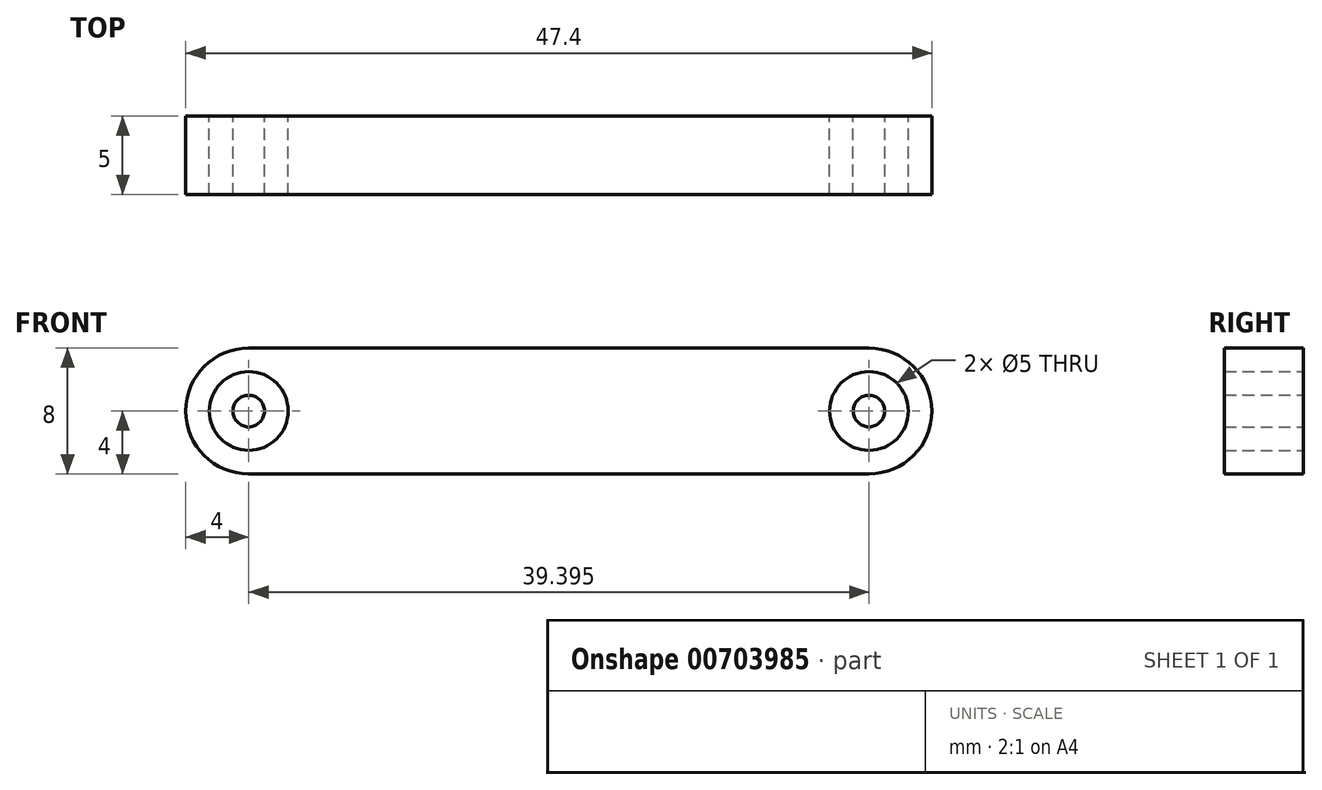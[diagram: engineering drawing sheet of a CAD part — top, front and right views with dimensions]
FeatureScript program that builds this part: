
annotation { "Feature Type Name" : "Feature", "Feature Type Description" : "" }
export const myFeature = defineFeature(function(context is Context, id is Id, definition is map)
    precondition{}
    {
        {
            var Q0;
            Q0=qCreatedBy(makeId("Front.planeOp"),FACE);
            var sketch = newSketch(context, id + "F0", { "sketchPlane" : qUnion([Q0])});
            skCircle(sketch, "E0", {"center": v(0, 0) * mm, "radius": 2.5 * mm});
            skCircle(sketch, "E1", {"center": v(39.4, 0) * mm, "radius": 1 * mm});
            skCircle(sketch, "E2", {"center": v(0, 0) * mm, "radius": 1 * mm});
            skCircle(sketch, "E3", {"center": v(39.4, 0) * mm, "radius": 2.5 * mm});
            skArc(sketch, "E4", {"start": v(0, -4) * mm, "mid": v(-4, 0) * mm, "end": v(0, 4) * mm});
            skArc(sketch, "E5", {"start": v(39.4, -4) * mm, "mid": v(43.4, 0) * mm, "end": v(39.4, 4) * mm});
            skLineSegment(sketch, "E6", {"start": v(0, 4) * mm, "end": v(39.4, 4) * mm});
            skLineSegment(sketch, "E7", {"start": v(0, -4) * mm, "end": v(39.4, -4) * mm});
            skSolve(sketch);
        }
        {
            var Q0;
            Q0=makeQuery(id+"F0.imprint","IMPRINT",FACE,{"disambiguationData":[TD([[makeQuery(id+"F0.imprint","IMPRINT",EDGE,{"derivedFrom":sQuery(id+"F0.wireOp",EDGE,"E0")}),-1.0]])]});
            var Q1;
            Q1=makeQuery(id+"F0.imprint","IMPRINT",FACE,{"disambiguationData":[TD([[makeQuery(id+"F0.imprint","IMPRINT",EDGE,{"derivedFrom":sQuery(id+"F0.wireOp",EDGE,"E2")}),1.0]])]});
            var Q2;
            Q2=makeQuery(id+"F0.imprint","IMPRINT",FACE,{"disambiguationData":[TD([[makeQuery(id+"F0.imprint","IMPRINT",EDGE,{"derivedFrom":sQuery(id+"F0.wireOp",EDGE,"E1")}),1.0]])]});
            extrude(context, id + "F1", {"entities" : qUnion([Q0, Q1, Q2]), "depth" : 5 * mm, "offsetDistance" : 25 * mm});
        }
    });
